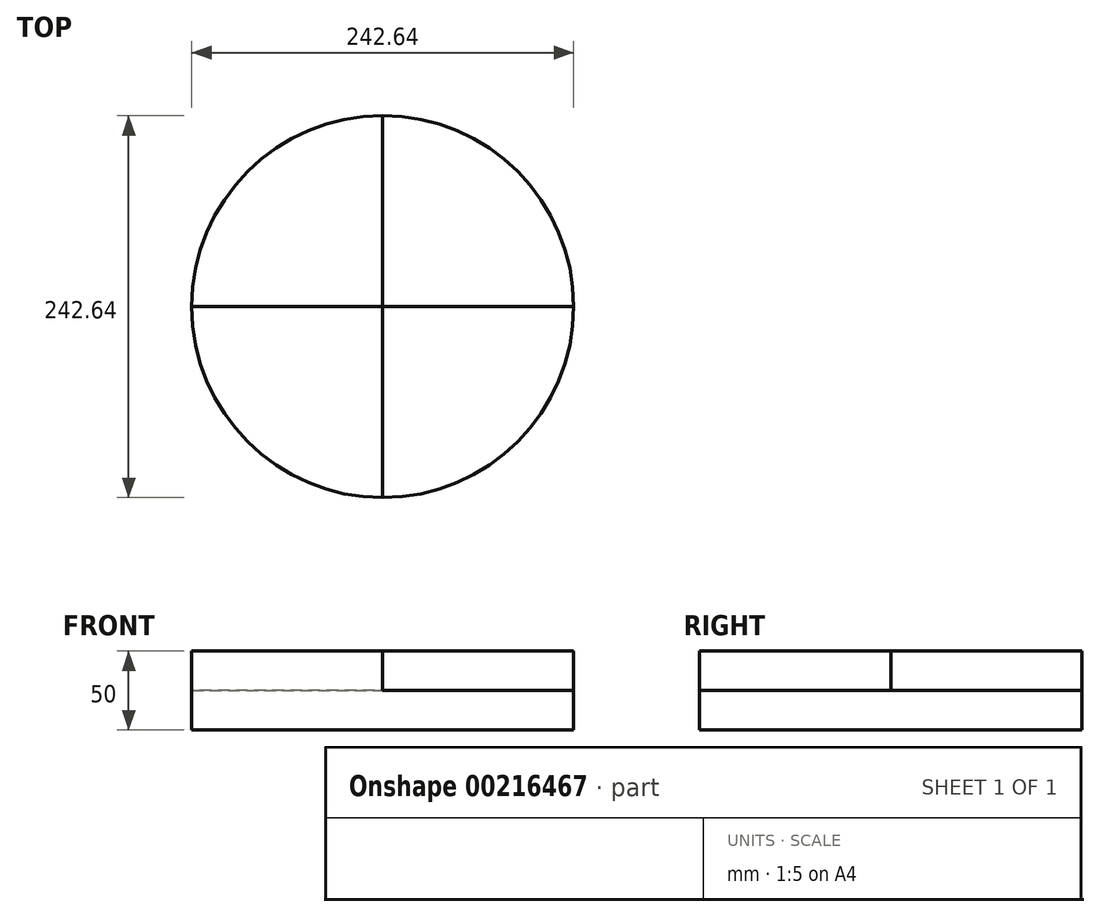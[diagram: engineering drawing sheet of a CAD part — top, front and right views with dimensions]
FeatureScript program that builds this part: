
annotation { "Feature Type Name" : "Feature", "Feature Type Description" : "" }
export const myFeature = defineFeature(function(context is Context, id is Id, definition is map)
    precondition{}
    {
        {
            var Q0;
            Q0=qCreatedBy(makeId("Top.planeOp"),FACE);
            var sketch = newSketch(context, id + "F0", { "sketchPlane" : qUnion([Q0])});
            skCircle(sketch, "E0", {"center": v(0, 0) * mm, "radius": 121.32 * mm});
            skLineSegment(sketch, "E1", {"start": v(0, 121.32) * mm, "end": v(0, -121.32) * mm});
            skLineSegment(sketch, "E2", {"start": v(-121.32, 0) * mm, "end": v(121.32, 0) * mm});
            skSolve(sketch);
        }
        {
            var Q0;
            Q0=qSketchRegion(id+"F0",true);
            extrude(context, id + "F1", {"entities" : qUnion([Q0]), "oppositeDirection" : true, "depth" : 25 * mm});
        }
        {
            var Q0;
            {var subQ1=sQuery(id+"F0.wireOp",EDGE,"E1");var subQ3=sQuery(id+"F0.wireOp",EDGE,"E0");var subQ5=makeQuery(id+"F0.imprint","INTERSECT",VERTEX,{"disambiguationData":[OD(1.0)],"derivedFrom":[subQ3,subQ1]});Q0=makeQuery(id+"F0.imprint","IMPRINT",FACE,{"disambiguationData":[TD([[makeQuery(id+"F0.imprint","IMPRINT",EDGE,{"disambiguationData":[TD([[subQ5,1.0]])],"derivedFrom":subQ3}),1.0]])]});}
            extrude(context, id + "F2", {"entities" : qUnion([Q0]), "operationType" : NewBodyOperationType.ADD, "depth" : 25 * mm});
        }
        {
            var Q0;
            {var subQ1=sQuery(id+"F0.wireOp",EDGE,"E1");var subQ3=sQuery(id+"F0.wireOp",EDGE,"E0");var subQ5=makeQuery(id+"F0.imprint","INTERSECT",VERTEX,{"disambiguationData":[OD(0.0)],"derivedFrom":[subQ3,subQ1]});Q0=makeQuery(id+"F0.imprint","IMPRINT",FACE,{"disambiguationData":[TD([[makeQuery(id+"F0.imprint","IMPRINT",EDGE,{"disambiguationData":[TD([[subQ5,1.0]])],"derivedFrom":subQ3}),1.0]])]});}
            extrude(context, id + "F3", {"entities" : qUnion([Q0]), "depth" : 25 * mm});
        }
    });
